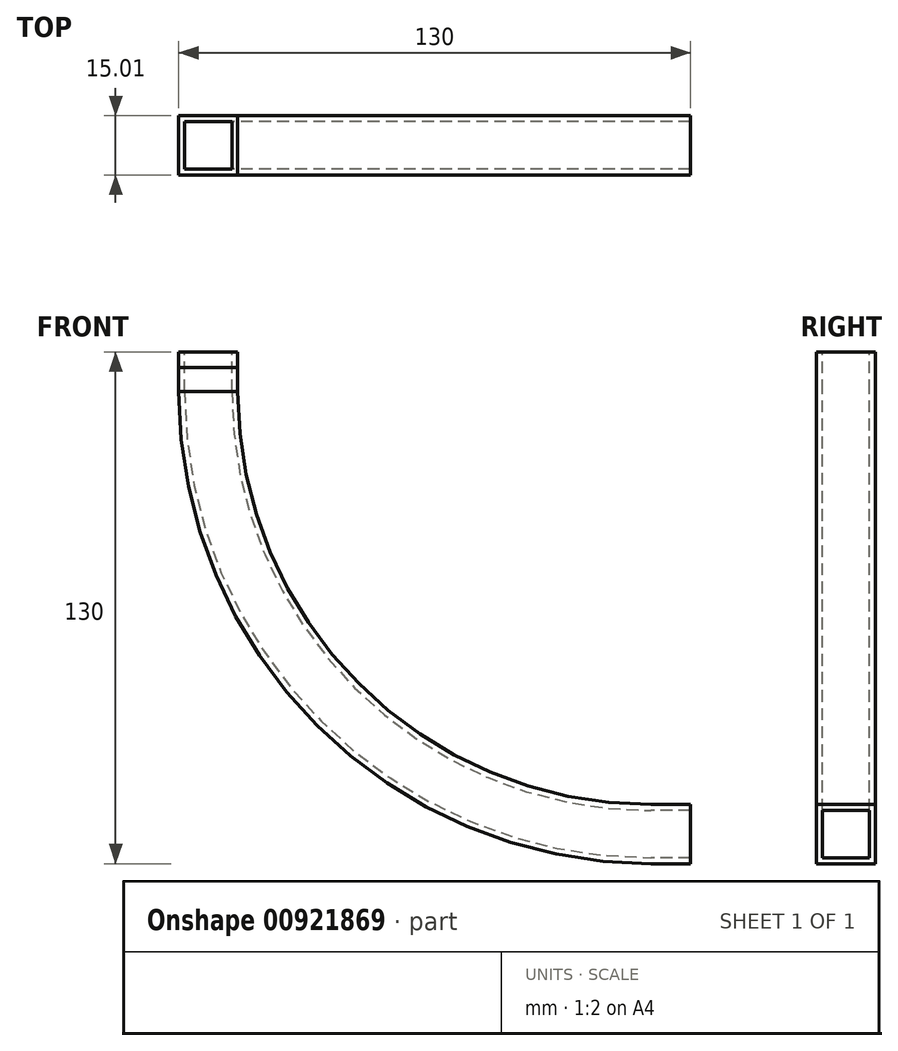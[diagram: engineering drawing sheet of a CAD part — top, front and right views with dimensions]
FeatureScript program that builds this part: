
annotation { "Feature Type Name" : "Feature", "Feature Type Description" : "" }
export const myFeature = defineFeature(function(context is Context, id is Id, definition is map)
    precondition{}
    {
        {
            var Q0;
            Q0=qCreatedBy(makeId("Front.planeOp"),FACE);
            var sketch = newSketch(context, id + "F0", { "sketchPlane" : qUnion([Q0])});
            skArc(sketch, "E0", {"start": v(-120, 0) * mm, "mid": v(-84.85, -84.85) * mm, "end": v(0, -120) * mm});
            skArc(sketch, "E1", {"start": v(-105, 0) * mm, "mid": v(-74.25, -74.25) * mm, "end": v(0, -105) * mm});
            skLineSegment(sketch, "E2", {"start": v(-120, 0) * mm, "end": v(-105, 0) * mm});
            skLineSegment(sketch, "E3", {"start": v(0, -105) * mm, "end": v(0, -120) * mm});
            skSolve(sketch);
        }
        {
            var Q0;
            Q0=makeQuery(id+"F0.imprint","IMPRINT",FACE,{"disambiguationData":[TD([[makeQuery(id+"F0.imprint","IMPRINT",EDGE,{"derivedFrom":sQuery(id+"F0.wireOp",EDGE,"E0")}),1.0]])]});
            extrude(context, id + "F1", {"entities" : qUnion([Q0]), "depth" : 15 * mm, "offsetDistance" : 25 * mm});
        }
        {
            var Q0;
            Q0=makeQuery(id+"F1.opExtrude","SWEPT_FACE",FACE,{"disambiguationData":[OSD([sQuery(id+"F0.wireOp",EDGE,"E2")])]});
            extrude(context, id + "F2", {"entities" : qUnion([Q0]), "operationType" : NewBodyOperationType.ADD, "depth" : 10 * mm, "offsetDistance" : 25 * mm});
        }
        {
            var Q0;
            Q0=makeQuery(id+"F1.opExtrude","SWEPT_FACE",FACE,{"disambiguationData":[OSD([sQuery(id+"F0.wireOp",EDGE,"E3")])]});
            extrude(context, id + "F3", {"entities" : qUnion([Q0]), "operationType" : NewBodyOperationType.ADD, "depth" : 10 * mm, "offsetDistance" : 25 * mm});
        }
        {
            var Q0;
            {var subQ0=sQuery(id+"F0.wireOp",EDGE,"E3");var subQ1=sQuery(id+"F0.wireOp",EDGE,"E2");Q0=makeQuery(id+"F3.boolean.opBoolean","MERGE",FACE,{"derivedFrom":[makeQuery(id+"F2.boolean.opBoolean","MERGE",FACE,{"derivedFrom":[makeQuery(id+"F1.opExtrude","CAP_FACE",FACE,{"disambiguationData":[OSD([sQuery(id+"F0.wireOp",EDGE,"E0"),sQuery(id+"F0.wireOp",EDGE,"E1"),subQ1,subQ0])],"isStart":false}),makeQuery(id+"F2.opExtrude","SWEPT_FACE",FACE,{"disambiguationData":[OSD([subQ1]),TDD([makeQuery(id+"F1.opExtrude","CAP_EDGE",EDGE,{"disambiguationData":[OSD([subQ1])],"isStart":false})])]})]}),makeQuery(id+"F3.opExtrude","SWEPT_FACE",FACE,{"disambiguationData":[OSD([subQ0]),TDD([makeQuery(id+"F1.opExtrude","CAP_EDGE",EDGE,{"disambiguationData":[OSD([subQ0])],"isStart":false})])]})]});}
            var sketch = newSketch(context, id + "F4", { "sketchPlane" : qUnion([Q0])});
            skLineSegment(sketch, "E4", {"start": v(-120, 0) * mm, "end": v(-105, 0) * mm});
            skSolve(sketch);
        }
        {
            var Q0;
            Q0=makeQuery(id+"F4.imprint","IMPRINT",FACE,{"disambiguationData":[TD([[makeQuery(id+"F4.imprint","IMPRINT",EDGE,{"derivedFrom":sQuery(id+"F4.wireOp",EDGE,"E4")}),1.0]])]});
            extrude(context, id + "F5", {"entities" : qUnion([Q0]), "operationType" : NewBodyOperationType.ADD, "depth" : 0.01 * mm, "offsetDistance" : 25 * mm});
        }
        {
            var Q0;
            Q0=makeQuery(id+"F5.opExtrude","CAP_FACE",FACE,{"disambiguationData":[OSD([sQuery(id+"F0.wireOp",EDGE,"E0"),sQuery(id+"F0.wireOp",EDGE,"E1"),sQuery(id+"F0.wireOp",EDGE,"E2"),sQuery(id+"F4.wireOp",EDGE,"E4")])],"isStart":false});
            var sketch = newSketch(context, id + "F6", { "sketchPlane" : qUnion([Q0])});
            skLineSegment(sketch, "E5.bottom", {"start": v(-120, 0) * mm, "end": v(-105, 0) * mm});
            skLineSegment(sketch, "E5.top", {"start": v(-120, 6) * mm, "end": v(-105, 6) * mm});
            skLineSegment(sketch, "E5.left", {"start": v(-120, 0) * mm, "end": v(-120, 6) * mm});
            skLineSegment(sketch, "E5.right", {"start": v(-105, 0) * mm, "end": v(-105, 6) * mm});
            skSolve(sketch);
        }
        {
            var Q0;
            {var subQ0=sQuery(id+"F6.wireOp",EDGE,"E5.top");Q0=makeQuery(id+"F6.imprint","IMPRINT",FACE,{"disambiguationData":[TD([[makeQuery(id+"F6.imprint","IMPRINT",EDGE,{"derivedFrom":subQ0}),1.0]])]});}
            extrude(context, id + "F7", {"entities" : qUnion([Q0]), "operationType" : NewBodyOperationType.REMOVE, "oppositeDirection" : true, "depth" : 0.01 * mm, "offsetDistance" : 25 * mm});
        }
        {
            var Q0;
            Q0=makeQuery(id+"F3.opExtrude","CAP_FACE",FACE,{"disambiguationData":[OSD([sQuery(id+"F0.wireOp",EDGE,"E3")])],"isStart":false});
            var sketch = newSketch(context, id + "F8", { "sketchPlane" : qUnion([Q0])});
            skPoint(sketch, "E6", {"position": v(-7.5, -112.5) * mm});
            skPoint(sketch, "E7.orphan", {"position": v(-7.5, -105) * mm});
            skPoint(sketch, "E8.orphan", {"position": v(-15, -112.5) * mm});
            skPoint(sketch, "E9.start.orphan", {"position": v(0, -112.5) * mm});
            skPoint(sketch, "E10.end.orphan", {"position": v(-7.5, -120) * mm});
            skLineSegment(sketch, "E11.bottom", {"start": v(-1.5, -118.5) * mm, "end": v(-13.5, -118.5) * mm});
            skLineSegment(sketch, "E11.top", {"start": v(-1.5, -106.5) * mm, "end": v(-13.5, -106.5) * mm});
            skLineSegment(sketch, "E11.left", {"start": v(-1.5, -118.5) * mm, "end": v(-1.5, -106.5) * mm});
            skLineSegment(sketch, "E11.right", {"start": v(-13.5, -118.5) * mm, "end": v(-13.5, -106.5) * mm});
            skSolve(sketch);
        }
        {
            var Q0;
            Q0=makeQuery(id+"F8.imprint","IMPRINT",FACE,{"disambiguationData":[TD([[makeQuery(id+"F8.imprint","IMPRINT",EDGE,{"derivedFrom":sQuery(id+"F8.wireOp",EDGE,"E11.bottom")}),-1.0]])]});
            var Q1;
            Q1=makeQuery(id+"F1.opExtrude","CAP_EDGE",EDGE,{"disambiguationData":[OSD([sQuery(id+"F0.wireOp",EDGE,"E1")])],"isStart":true});
            var Q2;
            {var subQ0=sQuery(id+"F0.wireOp",EDGE,"E2");var subQ1=sQuery(id+"F0.wireOp",EDGE,"E1");Q2=makeQuery(id+"F2.opExtrude","SWEPT_EDGE",EDGE,{"disambiguationData":[OSD([subQ1,subQ0]),TDD([makeQuery(id+"F1.opExtrude","CAP_VERTEX",VERTEX,{"disambiguationData":[OSD([subQ1,subQ0])],"isStart":true})])]});}
            var Q3;
            {var subQ0=sQuery(id+"F0.wireOp",EDGE,"E3");var subQ1=sQuery(id+"F0.wireOp",EDGE,"E1");Q3=makeQuery(id+"F3.opExtrude","SWEPT_EDGE",EDGE,{"disambiguationData":[OSD([subQ1,subQ0]),TDD([makeQuery(id+"F1.opExtrude","CAP_VERTEX",VERTEX,{"disambiguationData":[OSD([subQ1,subQ0])],"isStart":true})])]});}
            sweep(context, id + "F9", {"operationType" : NewBodyOperationType.REMOVE, "profiles" : qUnion([Q0]), "path" : qUnion([Q1, Q2, Q3])});
        }
    });
